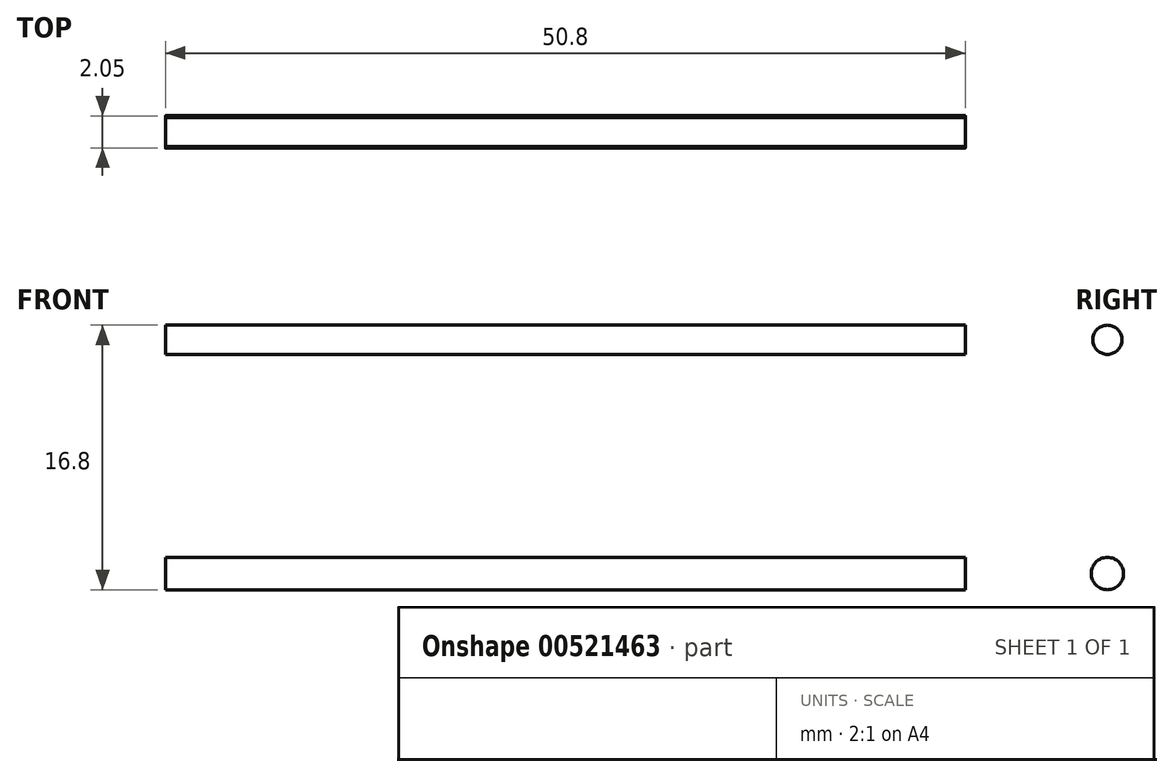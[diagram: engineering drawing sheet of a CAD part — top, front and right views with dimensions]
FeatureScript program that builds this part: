
annotation { "Feature Type Name" : "Feature", "Feature Type Description" : "" }
export const myFeature = defineFeature(function(context is Context, id is Id, definition is map)
    precondition{}
    {
        {
            var Q0;
            Q0=qCreatedBy(makeId("Front.planeOp"),FACE);
            var sketch = newSketch(context, id + "F0", { "sketchPlane" : qUnion([Q0])});
            skLineSegment(sketch, "E0", {"start": v(-34.2, 0) * mm, "end": v(-26.54, 0) * mm});
            skLineSegment(sketch, "E1", {"start": v(-26.54, 0) * mm, "end": v(-22.55, 23.56) * mm});
            skLineSegment(sketch, "E2", {"start": v(-22.55, 23.56) * mm, "end": v(-28.54, 24.57) * mm});
            skLineSegment(sketch, "E3", {"start": v(-28.54, 24.57) * mm, "end": v(-29.3, 20.14) * mm});
            skSolve(sketch);
        }
        {
            var Q0;
            Q0 = qSketchRegion(id + "F0", true);
            var Q1;
            Q1=sQuery(id+"F0.wireOp",EDGE,"E3");
            var Q2;
            Q2=sQuery(id+"F0.wireOp",EDGE,"E2");
            var Q3;
            Q3=sQuery(id+"F0.wireOp",EDGE,"E1");
            var Q4;
            Q4=sQuery(id+"F0.wireOp",EDGE,"E0");
            extrude(context, id + "F1", {"entities" : qUnion([Q0]), "bodyType" : ToolBodyType.SURFACE, "surfaceEntities" : qUnion([Q1, Q2, Q3, Q4]), "depth" : 51.05 * mm, "offsetDistance" : 25.4 * mm, "hasSecondDirection" : true, "secondDirectionOppositeDirection" : true, "secondDirectionDepth" : 50.8 * mm});
        }
        {
            var Q0;
            Q0=makeQuery(id+"F1.opExtrude","SWEPT_BODY",BODY,{"disambiguationData":[OSD([sQuery(id+"F0.wireOp",EDGE,"E0")])]});
            var Q1;
            Q1=qCreatedBy(makeId("Right.planeOp"),FACE);
            mirror(context, id + "F2", {"entities" : qUnion([Q0]), "mirrorPlane" : qUnion([Q1])});
        }
        {
            var Q0;
            Q0=qCreatedBy(makeId("Right.planeOp"),FACE);
            var sketch = newSketch(context, id + "F3", { "sketchPlane" : qUnion([Q0])});
            skCircle(sketch, "E4", {"center": v(-48.24, 17.18) * mm, "radius": 0.93 * mm});
            skCircle(sketch, "E5", {"center": v(-48.24, 2.33) * mm, "radius": 1.03 * mm});
            skSolve(sketch);
        }
        {
            var Q0;
            Q0 = qSketchRegion(id + "F3", true);
            extrude(context, id + "F4", {"entities" : qUnion([Q0]), "depth" : 25.4 * mm, "offsetDistance" : 25.4 * mm, "hasSecondDirection" : true, "secondDirectionOppositeDirection" : true, "secondDirectionDepth" : 25.4 * mm});
        }
    });
